# Revit family: CONV_Flokk_DmstcChrs_RBMNoorUp6090
name_source: partatom
category: Furniture
revit_build: Autodesk Revit 2015 (Build: 20140606_1530(x64)
units: mm (PartAtom-declared; Revit-internal decimal feet)

## types (1)
- CONV_Flokk_DmstcChrs_RBMNoorUp6090
    AssetType = Movable
    BIMObjectName = CONV_Flokk_OffcChrs_RBMNoorUp6090
    Brand = RBM
    Category = Meeting chair
    Collection = RBM Noor Up
    Color = Various
    ConvergoRefNr = 0119-1802-0043-NO
    Cost = 0 $
    Designer = StokkeAustad, Form Us With Love, Susanne Gronlund, Scandinavian Business Seating
    DurationUnit = Year
    ExpiringDate = 08/2018
    Features = Armrests, modular structure
armrests (optional extra), armrest height, armrest width,
seat height, seat depth, lumbar support, tilt resistance/HÅG
inBalance™, lockable tilt and foot support
    HighestSeatingHeight = 640 mm  [stored 2.09974 ft]
    IfcExportAs = IfcFurnishingElementType
    IfcExportType = CHAIR
    LowestSeatingHeight = 640 mm  [stored 2.09974 ft]
    MainColor = Various
    Manufacturer = Flokk
    ManufacturerName = Flokk
    ManufacturerURL = https://www.flokk.com
    Material = Polypropylene, metal
    Model = RBM Noor Up 6090
    ModelNumber = 6090
    NBSDescription = Stacking chairs
    NBSReference = 45-35-20/355
    Name = OffcChrs_RBMNoorUp6090
    NominalDepth = 545 mm  [stored 1.78806 ft]
    NominalHeight = 1034 mm
    NominalLength = 564 mm
    OfficeChairTertiaryMaterial = Plastic, Opaque Black
    ProductInformation = RBM Noor Up is our medium-high model. With sitting height at 63 centimetres, it’s the perfect height for coffee shops, breakfast bars or any other bustling, communal spaces where conversations flow and the atmosphere is dynamic. A wide range of colours are available for the polypropylene shell, which you can mix-and-match with various steel base colours. The model is stackable and armrests are optional.
    SeatingHeight = 640 mm  [stored 2.09974 ft]
    Shape = Sculptured
    Size = 564x545x1030 mm
    URL = https://www.flokk.com
    Uniclass2 = Pr_40_50_12_85
    Uniclass2015Description = Stools
    Uniclass2015Reference = Pr_40_50_12_85
    Version = 1
    VersionDate = 21/03/2018
    WarrantyDurationUnit = Year
    Weight = 7.7 kg

note: [stored X ft] marks values corroborated as IEEE doubles in the binary element streams (Revit-internal decimal feet)

## geometry (parser evidence)
native form markers: Sweep x13
no freeform markers — native parametric forms only
